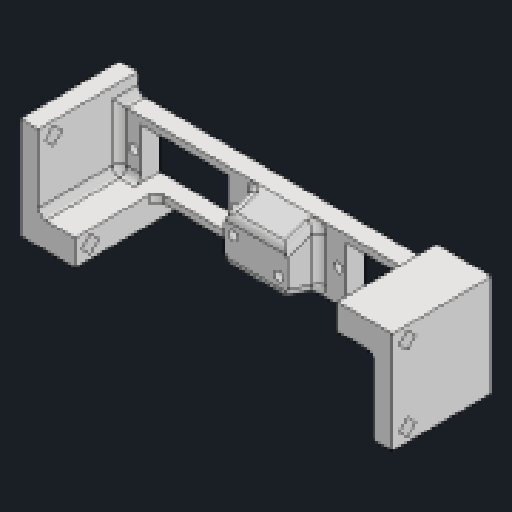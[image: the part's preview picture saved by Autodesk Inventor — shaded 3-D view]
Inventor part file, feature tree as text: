
AUTODESK INVENTOR PART (.ipt)
format: ipt  version: 2023.2 (Build 272271030, 271C)  size: 711,680 bytes
history: native  units: mm
features: sketch x7, projected_geometry x6, extrude x5, chamfer x3, hole x2, other x2, fillet x1
ambient origin geometry x8: Origin, YZ Plane, XZ Plane, XY Plane, X Axis, Y Axis, Z Axis, Center Point
bodies: Solid1 (feature_tree)
feature tree (26):
  extrude  "Extrusion1"  Depth=27.5mm
  extrude  "Extrusion2"  Depth=13.5mm
  hole  "Hole1"  [1 undecoded]
  extrude  "Extrusion4"  Depth=7.0mm
  extrude  "Extrusion3"  Depth=7.0mm
  chamfer  "Chamfer1"  Distance=5.0mm
  hole  "Hole2"  [1 undecoded]
  sketch  "Sketch6"  dims[d11=5.0mm]
  fillet  "Fillet2"  Radius=27.8mm
  extrude  "Extrusion5"  Depth=3.5mm
  other  "Work Axis1"
  other  "Work Axis2"
  chamfer  "Chamfer3"  Distance=17.0mm
  chamfer  "Chamfer4"  Distance=8.5mm
  sketch  "Sketch1"  dims[d0=101.0mm d1=27.5mm]
  sketch  "Sketch2"  dims[d2=7.0mm d3=13.5mm]
  projected_geometry  "Projected Loop1"
  sketch  "Sketch3"  dims[d4=11.0mm d5=11.0mm]
  projected_geometry  "Projected Loop2"
  sketch  "Sketch4"  dims[d6=23.5mm d7=7.0mm]
  projected_geometry  "Projected Loop3"
  sketch  "Sketch5"  dims[d8=5.0mm d9=0.0mm d10=7.0mm]
  projected_geometry  "Projected Loop4"
  projected_geometry  "Projected Loop5"
  sketch  "Sketch7"  dims[d12=15.0mm d13=5.0mm d14=22.0mm d15=0.0mm d16=27.8mm d17=2.5mm d18=6.0mm d19=5.5mm d20=25.45mm d21=90.0deg d22=8.0mm d23=20.594885mm d24=7.0mm d25=17.0mm d26=8.5mm d27=0.0mm d28=3.0mm d29=8.5mm d30=45.0deg d31=6.6mm d32=16.5mm d33=6.6mm d34=12.125mm d35=12.125mm d36=2.5mm d37=6.0mm d38=3.7mm d39=3.5mm d40=90.0deg d41=8.0mm d42=20.594885mm d43=20.5mm d45=3.5mm d46=3.5mm d58=22.95mm d59=2.0mm d60=2.0mm d61=22.0mm d62=0.0mm d63=2.0mm d64=3.3mm d65=0.0mm d66=0.0mm d67=0.5mm d68=2.0mm d69=45.0deg d70=1.0mm d71=2.0mm d72=45.0deg]
  projected_geometry  "Projected Loop6"
note: 2 required parameter values undecoded (feature->parameter linkage not recoverable at this tier; creation-order binding heuristic only, values carry confidence <= 0.55)
